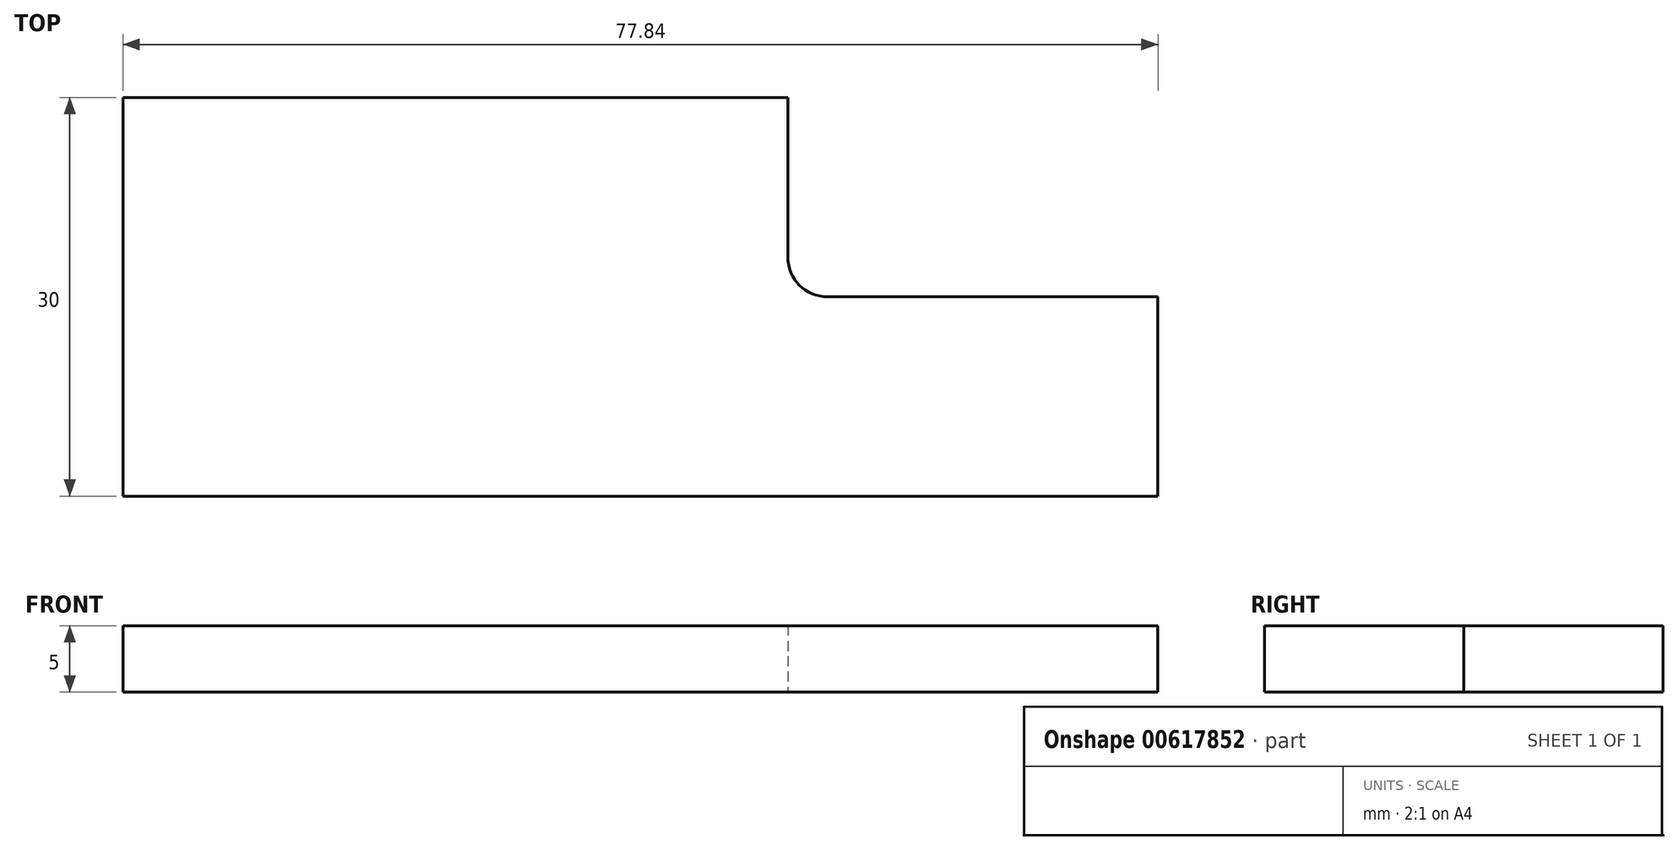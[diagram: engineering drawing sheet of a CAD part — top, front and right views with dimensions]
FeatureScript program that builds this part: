
annotation { "Feature Type Name" : "Feature", "Feature Type Description" : "" }
export const myFeature = defineFeature(function(context is Context, id is Id, definition is map)
    precondition{}
    {
        {
            var Q0;
            Q0=qCreatedBy(makeId("Top.planeOp"),FACE);
            var sketch = newSketch(context, id + "F0", { "sketchPlane" : qUnion([Q0])});
            skLineSegment(sketch, "E0.bottom", {"start": v(-25, -15) * mm, "end": v(25, -15) * mm});
            skLineSegment(sketch, "E0.top", {"start": v(-25, 15) * mm, "end": v(25, 15) * mm});
            skLineSegment(sketch, "E0.left", {"start": v(-25, -15) * mm, "end": v(-25, 15) * mm});
            skLineSegment(sketch, "E0.right", {"start": v(25, 3) * mm, "end": v(25, 15) * mm});
            skPoint(sketch, "E0.middle", {"position": v(0, 0) * mm});
            skLineSegment(sketch, "E1", {"start": v(25, -15) * mm, "end": v(52.84, -15) * mm});
            skLineSegment(sketch, "E2", {"start": v(52.84, -15) * mm, "end": v(52.84, 0) * mm});
            skLineSegment(sketch, "E3", {"start": v(52.84, 0) * mm, "end": v(28, 0) * mm});
            skPoint(sketch, "E4.newPointA", {"position": v(25, 0) * mm});
            skPoint(sketch, "E4.newPointB", {"position": v(25, -15) * mm});
            skArc(sketch, "E4.filletArc", {"start": v(25, 3) * mm, "mid": v(25.88, 0.88) * mm, "end": v(28, 0) * mm});
            skSolve(sketch);
        }
        {
            var Q0;
            Q0 = qSketchRegion(id + "F0", true);
            extrude(context, id + "F1", {"entities" : qUnion([Q0]), "depth" : 5 * mm, "offsetDistance" : 25 * mm});
        }
    });
